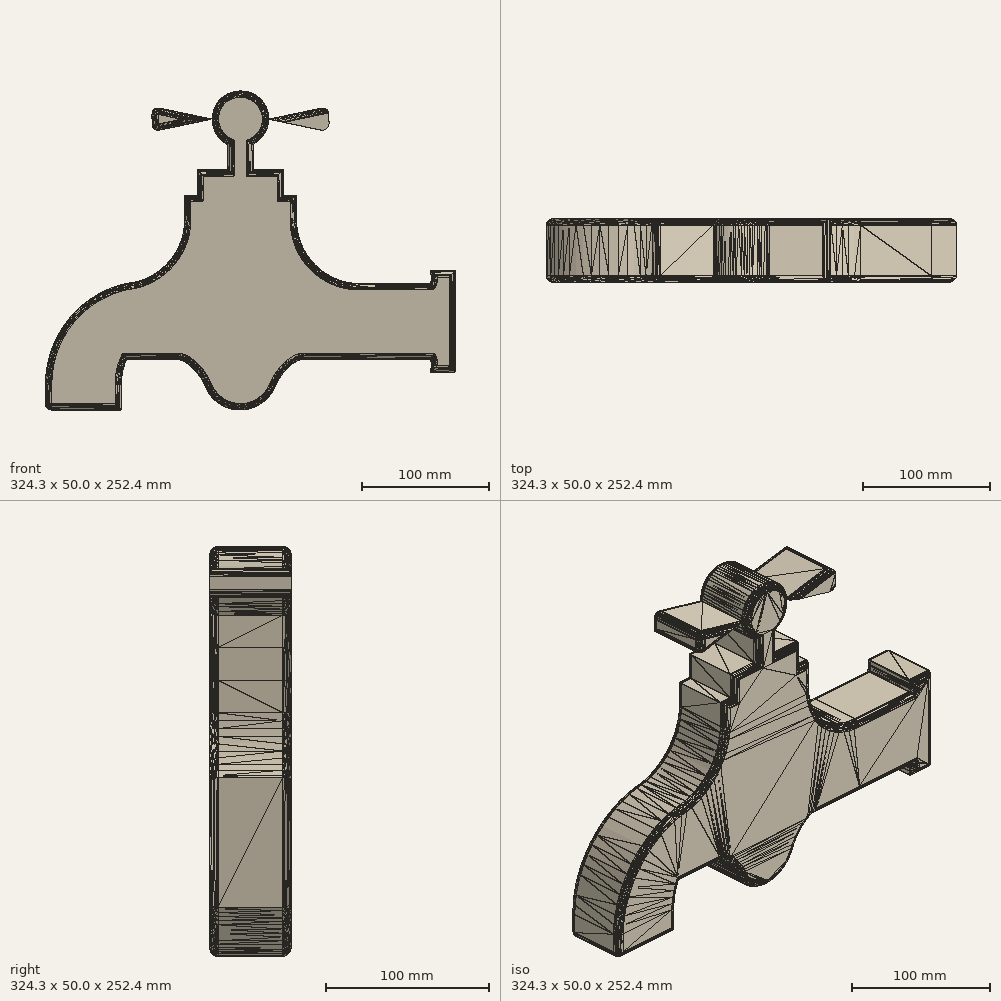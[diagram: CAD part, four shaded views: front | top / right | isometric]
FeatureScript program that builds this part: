
annotation { "Feature Type Name" : "Feature", "Feature Type Description" : "" }
export const myFeature = defineFeature(function(context is Context, id is Id, definition is map)
    precondition{}
    {
        {
            var Q0;
            Q0=qCreatedBy(makeId("Front.planeOp"),FACE);
            var sketch = newSketch(context, id + "F0", { "sketchPlane" : qUnion([Q0])});
            skLineSegment(sketch, "E0", {"start": v(0, 100) * mm, "end": v(0, -69.99) * mm, "construction": true});
            skPoint(sketch, "E1.first.point", {"position": v(0, 0) * mm});
            skLineSegment(sketch, "E2", {"start": v(-44.27, 100) * mm, "end": v(44.27, 100) * mm});
            skLineSegment(sketch, "E3", {"start": v(-44.27, 100) * mm, "end": v(-44.27, 80) * mm});
            skLineSegment(sketch, "E4", {"start": v(44.27, 100) * mm, "end": v(44.27, 80) * mm});
            skLineSegment(sketch, "E5", {"start": v(0, 100) * mm, "end": v(0, 193.4) * mm, "construction": true});
            skLineSegment(sketch, "E6", {"start": v(-34.27, 100) * mm, "end": v(-34.27, 120) * mm});
            skLineSegment(sketch, "E7", {"start": v(-34.27, 120) * mm, "end": v(0, 120) * mm});
            skLineSegment(sketch, "E8", {"start": v(-10, 120) * mm, "end": v(-10, 140) * mm});
            skLineSegment(sketch, "E9.MirrorCS", {"start": v(34.27, 100) * mm, "end": v(34.27, 120) * mm});
            skLineSegment(sketch, "E10.MirrorCS", {"start": v(34.27, 120) * mm, "end": v(0, 120) * mm});
            skLineSegment(sketch, "E11.MirrorCS", {"start": v(10, 120) * mm, "end": v(10, 140) * mm});
            skLineSegment(sketch, "E12", {"start": v(-70, 160) * mm, "end": v(70, 160) * mm, "construction": true});
            skArc(sketch, "E13", {"start": v(10, 140) * mm, "mid": v(0, 182.36) * mm, "end": v(-10, 140) * mm});
            skLineSegment(sketch, "E14", {"start": v(69.88, 170) * mm, "end": v(70, 150) * mm});
            skLineSegment(sketch, "E15", {"start": v(-70.07, 170) * mm, "end": v(-70, 150) * mm});
            skLineSegment(sketch, "E16", {"start": v(-70.07, 170) * mm, "end": v(-22.36, 160) * mm});
            skLineSegment(sketch, "E17", {"start": v(-70, 150) * mm, "end": v(-22.36, 160) * mm});
            skLineSegment(sketch, "E18", {"start": v(69.88, 170) * mm, "end": v(22.36, 160) * mm});
            skLineSegment(sketch, "E19", {"start": v(22.36, 160) * mm, "end": v(70, 150) * mm});
            skArc(sketch, "E20", {"start": v(44.27, 80) * mm, "mid": v(58.91, 44.64) * mm, "end": v(94.27, 30) * mm});
            skLineSegment(sketch, "E21", {"start": v(94.27, 30) * mm, "end": v(150, 30) * mm});
            skLineSegment(sketch, "E22", {"start": v(150, 30) * mm, "end": v(150, 0) * mm, "construction": true});
            skLineSegment(sketch, "E23", {"start": v(150, 40) * mm, "end": v(170, 40) * mm});
            skLineSegment(sketch, "E24", {"start": v(170, 40) * mm, "end": v(170, 0) * mm});
            skFitSpline(sketch, "E25", {"points": [v(150, 40) * mm, v(150, 30) * mm], "startDerivative": vector(3.62, -12.46) * mm, "endDerivative": vector(-4.3, -11.12) * mm});
            skLineSegment(sketch, "E26.MirrorCS", {"start": v(94.38, -30) * mm, "end": v(150, -30) * mm});
            skFitSpline(sketch, "E27.MirrorCS", {"points": [v(150, -40) * mm, v(150, -30) * mm], "startDerivative": vector(3.62, 12.46) * mm, "endDerivative": vector(-4.3, 11.12) * mm});
            skLineSegment(sketch, "E28.MirrorCS", {"start": v(150, -40) * mm, "end": v(170, -40) * mm});
            skLineSegment(sketch, "E29.MirrorCS", {"start": v(170, -40) * mm, "end": v(170, 0) * mm});
            skArc(sketch, "E30.MirrorCS", {"start": v(-44.27, 80) * mm, "mid": v(-58.91, 44.64) * mm, "end": v(-94.27, 30) * mm});
            skFitSpline(sketch, "E31", {"points": [v(50, -29.99) * mm, v(28.11, -50.47) * mm], "startDerivative": vector(-22.61, -0.1) * mm, "endDerivative": vector(-10.69, -26.35) * mm});
            skLineSegment(sketch, "E32", {"start": v(50, -29.99) * mm, "end": v(94.38, -30) * mm});
            skFitSpline(sketch, "E33.MirrorCS", {"points": [v(-50, -29.99) * mm, v(-28.11, -50.47) * mm], "startDerivative": vector(22.61, -0.1) * mm, "endDerivative": vector(10.69, -26.35) * mm});
            skLineSegment(sketch, "E34", {"start": v(13226.93, -29.99) * mm, "end": v(13181.02, -30.02) * mm, "construction": true});
            skArc(sketch, "E35", {"start": v(-28.11, -50.47) * mm, "mid": v(0, -69.99) * mm, "end": v(28.11, -50.47) * mm});
            skLineSegment(sketch, "E36", {"start": v(-50, -29.99) * mm, "end": v(-90, -29.99) * mm});
            skLineSegment(sketch, "E37", {"start": v(-44.27, 100) * mm, "end": v(-46.18, -69.99) * mm, "construction": true});
            skPoint(sketch, "E37.endSnap0", {"position": v(-46.18, 155) * mm});
            skLineSegment(sketch, "E38", {"start": v(-94.27, -70) * mm, "end": v(-154.27, -70) * mm});
            skLineSegment(sketch, "E39", {"start": v(-154.27, -70) * mm, "end": v(-154.27, -50) * mm});
            skArc(sketch, "E40", {"start": v(-89.81, 30.2) * mm, "mid": v(-136.16, 1.45) * mm, "end": v(-154.27, -50) * mm});
            skPoint(sketch, "E40.second.point", {"position": v(7.97, -31.96) * mm});
            skPoint(sketch, "E40.third.point", {"position": v(-41.46, -93.1) * mm});
            skLineSegment(sketch, "E41", {"start": v(-94.27, -70) * mm, "end": v(-94.27, -50) * mm});
            skArc(sketch, "E42", {"start": v(-90, -29.99) * mm, "mid": v(-93.19, -39.77) * mm, "end": v(-94.27, -50) * mm});
            skPoint(sketch, "E42.third.point", {"position": v(-94.27, -50) * mm});
            skSolve(sketch);
        }
        {
            var Q0;
            Q0 = qSketchRegion(id + "F0", true);
            extrude(context, id + "F1", {"entities" : qUnion([Q0]), "depth" : 50 * mm, "offsetDistance" : 25 * mm});
        }
        {
            var Q0;
            Q0=makeQuery(id+"F1.opExtrude","CAP_FACE",FACE,{"disambiguationData":[OSD([sQuery(id+"F0.wireOp",EDGE,"E2"),sQuery(id+"F0.wireOp",EDGE,"E3"),sQuery(id+"F0.wireOp",EDGE,"E4"),sQuery(id+"F0.wireOp",EDGE,"E6"),sQuery(id+"F0.wireOp",EDGE,"E7"),sQuery(id+"F0.wireOp",EDGE,"E8"),sQuery(id+"F0.wireOp",EDGE,"E9.MirrorCS"),sQuery(id+"F0.wireOp",EDGE,"E10.MirrorCS"),sQuery(id+"F0.wireOp",EDGE,"E11.MirrorCS"),sQuery(id+"F0.wireOp",EDGE,"E13"),sQuery(id+"F0.wireOp",EDGE,"E20"),sQuery(id+"F0.wireOp",EDGE,"E21"),sQuery(id+"F0.wireOp",EDGE,"E23"),sQuery(id+"F0.wireOp",EDGE,"E24"),sQuery(id+"F0.wireOp",EDGE,"E25"),sQuery(id+"F0.wireOp",EDGE,"E26.MirrorCS"),sQuery(id+"F0.wireOp",EDGE,"E27.MirrorCS"),sQuery(id+"F0.wireOp",EDGE,"E28.MirrorCS"),sQuery(id+"F0.wireOp",EDGE,"E29.MirrorCS"),sQuery(id+"F0.wireOp",EDGE,"E30.MirrorCS"),sQuery(id+"F0.wireOp",EDGE,"E31"),sQuery(id+"F0.wireOp",EDGE,"E32"),sQuery(id+"F0.wireOp",EDGE,"E33.MirrorCS"),sQuery(id+"F0.wireOp",EDGE,"E35"),sQuery(id+"F0.wireOp",EDGE,"E36"),sQuery(id+"F0.wireOp",EDGE,"E38"),sQuery(id+"F0.wireOp",EDGE,"E39"),sQuery(id+"F0.wireOp",EDGE,"E40"),sQuery(id+"F0.wireOp",EDGE,"E41"),sQuery(id+"F0.wireOp",EDGE,"E42")])],"isStart":true});
            var Q1;
            Q1=makeQuery(id+"F1.opExtrude","CAP_EDGE",EDGE,{"disambiguationData":[OSD([sQuery(id+"F0.wireOp",EDGE,"E35")])],"isStart":false});
            var Q2;
            Q2=makeQuery(id+"F1.opExtrude","CAP_EDGE",EDGE,{"disambiguationData":[OSD([sQuery(id+"F0.wireOp",EDGE,"E26.MirrorCS")])],"isStart":false});
            var Q3;
            Q3=makeQuery(id+"F1.opExtrude","CAP_EDGE",EDGE,{"disambiguationData":[OSD([sQuery(id+"F0.wireOp",EDGE,"E28.MirrorCS")])],"isStart":false});
            var Q4;
            Q4=makeQuery(id+"F1.opExtrude","CAP_EDGE",EDGE,{"disambiguationData":[OSD([sQuery(id+"F0.wireOp",EDGE,"E32")])],"isStart":false});
            var Q5;
            Q5=makeQuery(id+"F1.opExtrude","CAP_EDGE",EDGE,{"disambiguationData":[OSD([sQuery(id+"F0.wireOp",EDGE,"E31")])],"isStart":false});
            var Q6;
            Q6=makeQuery(id+"F1.opExtrude","CAP_EDGE",EDGE,{"disambiguationData":[OSD([sQuery(id+"F0.wireOp",EDGE,"E36")])],"isStart":false});
            var Q7;
            Q7=makeQuery(id+"F1.opExtrude","CAP_EDGE",EDGE,{"disambiguationData":[OSD([sQuery(id+"F0.wireOp",EDGE,"E38")])],"isStart":false});
            var Q8;
            Q8=makeQuery(id+"F1.opExtrude","SWEPT_EDGE",EDGE,{"disambiguationData":[OSD([sQuery(id+"F0.wireOp",EDGE,"E38"),sQuery(id+"F0.wireOp",EDGE,"E39")])]});
            var Q9;
            Q9=makeQuery(id+"F1.opExtrude","CAP_FACE",FACE,{"disambiguationData":[OSD([sQuery(id+"F0.wireOp",EDGE,"E2"),sQuery(id+"F0.wireOp",EDGE,"E3"),sQuery(id+"F0.wireOp",EDGE,"E4"),sQuery(id+"F0.wireOp",EDGE,"E6"),sQuery(id+"F0.wireOp",EDGE,"E7"),sQuery(id+"F0.wireOp",EDGE,"E8"),sQuery(id+"F0.wireOp",EDGE,"E9.MirrorCS"),sQuery(id+"F0.wireOp",EDGE,"E10.MirrorCS"),sQuery(id+"F0.wireOp",EDGE,"E11.MirrorCS"),sQuery(id+"F0.wireOp",EDGE,"E13"),sQuery(id+"F0.wireOp",EDGE,"E20"),sQuery(id+"F0.wireOp",EDGE,"E21"),sQuery(id+"F0.wireOp",EDGE,"E23"),sQuery(id+"F0.wireOp",EDGE,"E24"),sQuery(id+"F0.wireOp",EDGE,"E25"),sQuery(id+"F0.wireOp",EDGE,"E26.MirrorCS"),sQuery(id+"F0.wireOp",EDGE,"E27.MirrorCS"),sQuery(id+"F0.wireOp",EDGE,"E28.MirrorCS"),sQuery(id+"F0.wireOp",EDGE,"E29.MirrorCS"),sQuery(id+"F0.wireOp",EDGE,"E30.MirrorCS"),sQuery(id+"F0.wireOp",EDGE,"E31"),sQuery(id+"F0.wireOp",EDGE,"E32"),sQuery(id+"F0.wireOp",EDGE,"E33.MirrorCS"),sQuery(id+"F0.wireOp",EDGE,"E35"),sQuery(id+"F0.wireOp",EDGE,"E36"),sQuery(id+"F0.wireOp",EDGE,"E38"),sQuery(id+"F0.wireOp",EDGE,"E39"),sQuery(id+"F0.wireOp",EDGE,"E40"),sQuery(id+"F0.wireOp",EDGE,"E41"),sQuery(id+"F0.wireOp",EDGE,"E42")])],"isStart":false});
            var Q10;
            Q10=makeQuery(id+"F1.opExtrude","SWEPT_EDGE",EDGE,{"disambiguationData":[OSD([sQuery(id+"F0.wireOp",EDGE,"E14"),sQuery(id+"F0.wireOp",EDGE,"E18")])]});
            var Q11;
            Q11=makeQuery(id+"F1.opExtrude","SWEPT_EDGE",EDGE,{"disambiguationData":[OSD([sQuery(id+"F0.wireOp",EDGE,"E14"),sQuery(id+"F0.wireOp",EDGE,"E19")])]});
            var Q12;
            Q12=makeQuery(id+"F1.opExtrude","CAP_EDGE",EDGE,{"disambiguationData":[OSD([sQuery(id+"F0.wireOp",EDGE,"E18")])],"isStart":false});
            var Q13;
            Q13=makeQuery(id+"F1.opExtrude","CAP_EDGE",EDGE,{"disambiguationData":[OSD([sQuery(id+"F0.wireOp",EDGE,"E19")])],"isStart":true});
            var Q14;
            Q14=makeQuery(id+"F1.opExtrude","CAP_EDGE",EDGE,{"disambiguationData":[OSD([sQuery(id+"F0.wireOp",EDGE,"E18")])],"isStart":true});
            var Q15;
            Q15=makeQuery(id+"F1.opExtrude","CAP_EDGE",EDGE,{"disambiguationData":[OSD([sQuery(id+"F0.wireOp",EDGE,"E16")])],"isStart":true});
            var Q16;
            Q16=makeQuery(id+"F1.opExtrude","CAP_EDGE",EDGE,{"disambiguationData":[OSD([sQuery(id+"F0.wireOp",EDGE,"E15")])],"isStart":true});
            var Q17;
            Q17=makeQuery(id+"F1.opExtrude","CAP_EDGE",EDGE,{"disambiguationData":[OSD([sQuery(id+"F0.wireOp",EDGE,"E15")])],"isStart":false});
            var Q18;
            Q18=makeQuery(id+"F1.opExtrude","CAP_EDGE",EDGE,{"disambiguationData":[OSD([sQuery(id+"F0.wireOp",EDGE,"E16")])],"isStart":false});
            var Q19;
            Q19=makeQuery(id+"F1.opExtrude","CAP_EDGE",EDGE,{"disambiguationData":[OSD([sQuery(id+"F0.wireOp",EDGE,"E17")])],"isStart":false});
            var Q20;
            Q20=makeQuery(id+"F1.opExtrude","SWEPT_EDGE",EDGE,{"disambiguationData":[OSD([sQuery(id+"F0.wireOp",EDGE,"E15"),sQuery(id+"F0.wireOp",EDGE,"E16")])]});
            var Q21;
            Q21=makeQuery(id+"F1.opExtrude","SWEPT_EDGE",EDGE,{"disambiguationData":[OSD([sQuery(id+"F0.wireOp",EDGE,"E15"),sQuery(id+"F0.wireOp",EDGE,"E17")])]});
            fillet(context, id + "F2", {"entities" : qUnion([Q0, Q1, Q2, Q3, Q4, Q5, Q6, Q7, Q8, Q9, Q10, Q11, Q12, Q13, Q14, Q15, Q16, Q17, Q18, Q19, Q20, Q21]), "radius" : 5 * mm, "tangentPropagation" : true, "allowEdgeOverflow" : false});
        }
    });
